# Revit family: F131-48X28.5X42
name_source: partatom
category: Furniture Systems
units: mm (PartAtom-declared; Revit-internal decimal feet)

## family parameters
Always vertical = Yes
Cut with Voids When Loaded = No
Part Type = Normal
Room Calculation Point = No
Round Connector Dimension = Use Diameter
Shared = No
Work Plane-Based = No

## types (4) — shared parameters
6" Rectangle Leg = <By Category>
Back Fabric = <By Category>
Base = <By Category>
Caster = Default New Material(1)
Description = Cafe Series - Café Booth (Seat height 18")
Leg H = 0' - 6 1/2"
Manufacturer = FOMCORE
Mod Leg = <By Category>
Model = F131-48X28.5X42
Seat Fabric = <By Category>
Triangle Leg = <By Category>
URL = https://fomcore.com

## per-type parameters (varying)
| type | C6 | LEG OPTIONS | M6 | R6 | T6 |
| F131-48X28.5X42-C6 | Yes | 1 | No | No | No |
| F131-48X28.5X42-M6 | No | 2 | Yes | No | No |
| F131-48X28.5X42-R6 | No | 3 | No | Yes | No |
| F131-48X28.5X42-T6 | No | 4 | No | No | Yes |

## geometry (parser evidence)
native form markers: Sweep x2
no freeform markers — native parametric forms only
